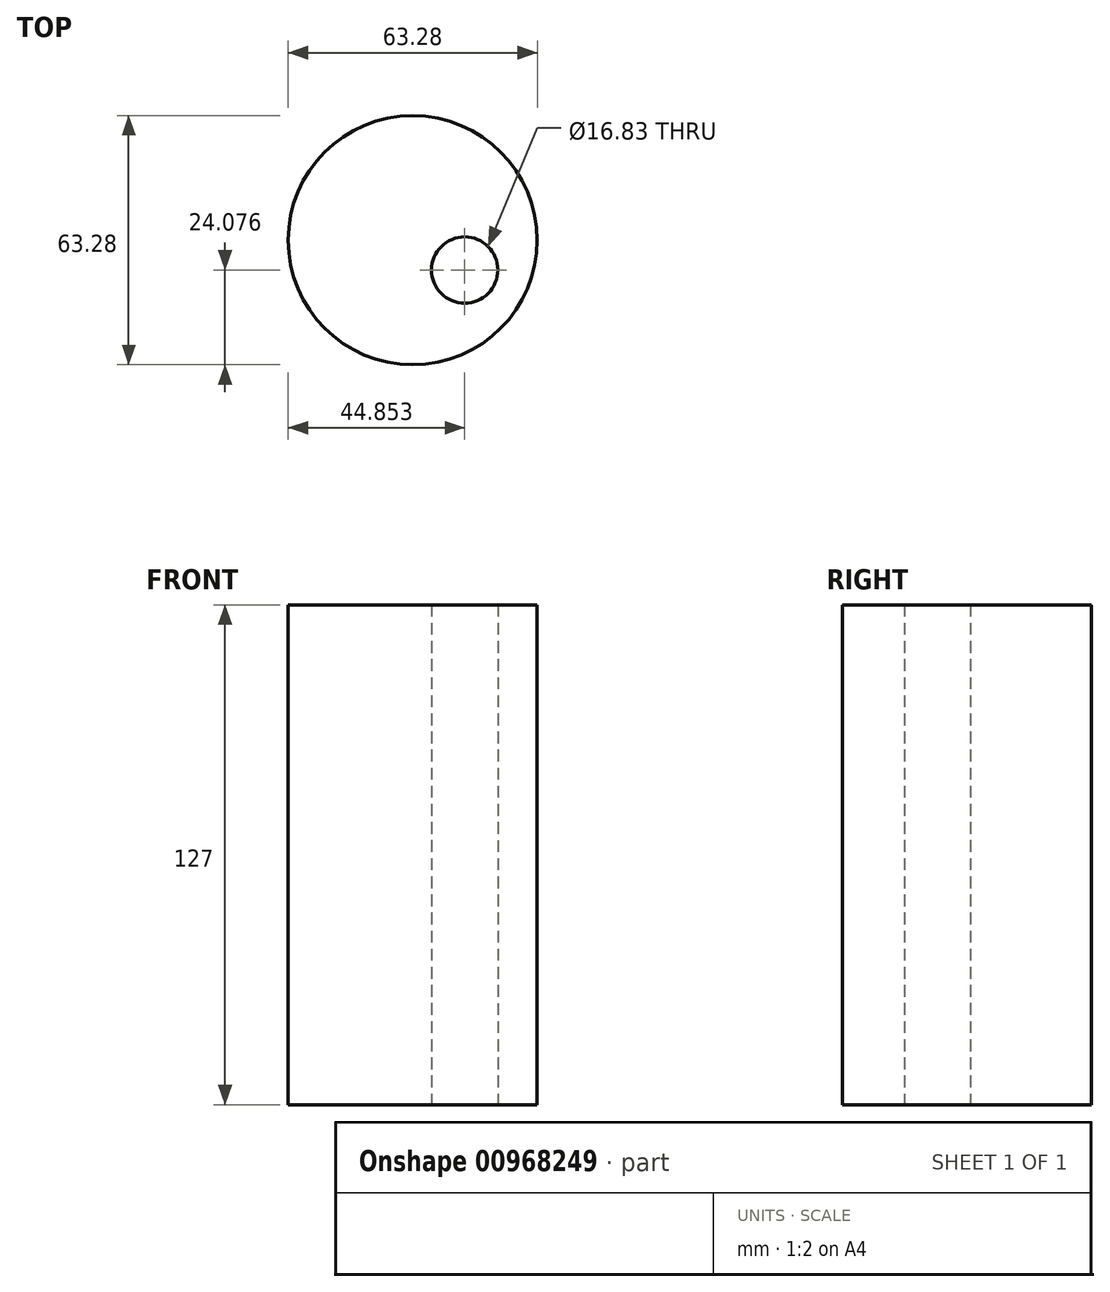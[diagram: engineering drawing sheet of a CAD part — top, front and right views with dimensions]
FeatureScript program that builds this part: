
annotation { "Feature Type Name" : "Feature", "Feature Type Description" : "" }
export const myFeature = defineFeature(function(context is Context, id is Id, definition is map)
    precondition{}
    {
        {
            var Q0;
            Q0=qCreatedBy(makeId("Top.planeOp"),FACE);
            var sketch = newSketch(context, id + "F0", { "sketchPlane" : qUnion([Q0])});
            skCircle(sketch, "E0", {"center": v(0, 0) * mm, "radius": 31.64 * mm});
            skCircle(sketch, "E1", {"center": v(13.21, -7.56) * mm, "radius": 8.42 * mm});
            skSolve(sketch);
        }
        {
            var Q0;
            Q0 = qSketchRegion(id + "F0", true);
            var Q1;
            Q1=makeQuery(id+"F0.imprint","IMPRINT",FACE,{"disambiguationData":[TD([[makeQuery(id+"F0.imprint","IMPRINT",EDGE,{"derivedFrom":sQuery(id+"F0.wireOp",EDGE,"E0")}),1.0]])]});
            extrude(context, id + "F1", {"entities" : qUnion([Q0, Q1]), "depth" : 127 * mm, "offsetDistance" : 25.4 * mm});
        }
    });
